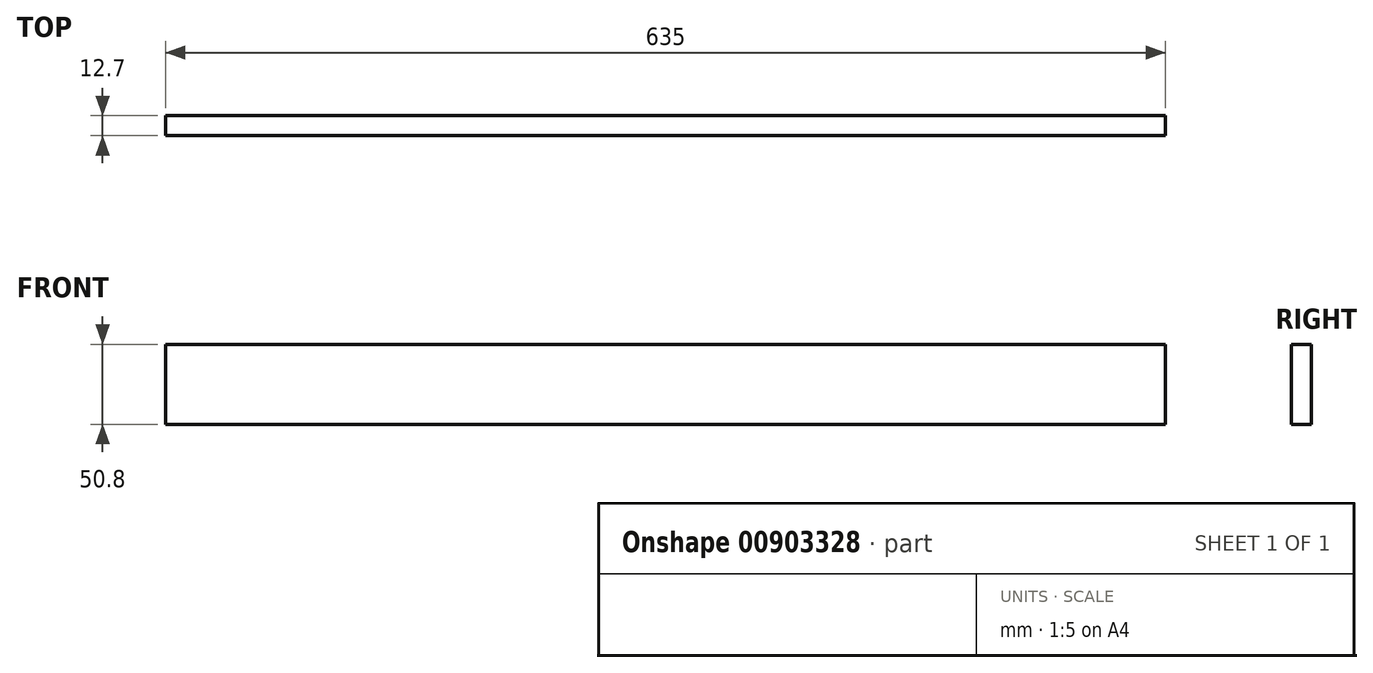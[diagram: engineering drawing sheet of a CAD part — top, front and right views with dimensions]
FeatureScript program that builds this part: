
annotation { "Feature Type Name" : "Feature", "Feature Type Description" : "" }
export const myFeature = defineFeature(function(context is Context, id is Id, definition is map)
    precondition{}
    {
        {
            var Q0;
            Q0=qCreatedBy(makeId("Right.planeOp"),FACE);
            var sketch = newSketch(context, id + "F0", { "sketchPlane" : qUnion([Q0])});
            skLineSegment(sketch, "E0.bottom", {"start": v(-25.21, 17.4) * mm, "end": v(-12.51, 17.4) * mm});
            skLineSegment(sketch, "E0.top", {"start": v(-25.21, -33.4) * mm, "end": v(-12.51, -33.4) * mm});
            skLineSegment(sketch, "E0.left", {"start": v(-25.21, 17.4) * mm, "end": v(-25.21, -33.4) * mm});
            skLineSegment(sketch, "E0.right", {"start": v(-12.51, 17.4) * mm, "end": v(-12.51, -33.4) * mm});
            skSolve(sketch);
        }
        {
            var Q0;
            Q0=makeQuery(id+"F0.imprint","IMPRINT",FACE,{"disambiguationData":[TD([[makeQuery(id+"F0.imprint","IMPRINT",EDGE,{"derivedFrom":sQuery(id+"F0.wireOp",EDGE,"E0.bottom")}),-1.0]])]});
            extrude(context, id + "F1", {"entities" : qUnion([Q0]), "depth" : 635 * mm, "offsetDistance" : 25.4 * mm});
        }
    });
